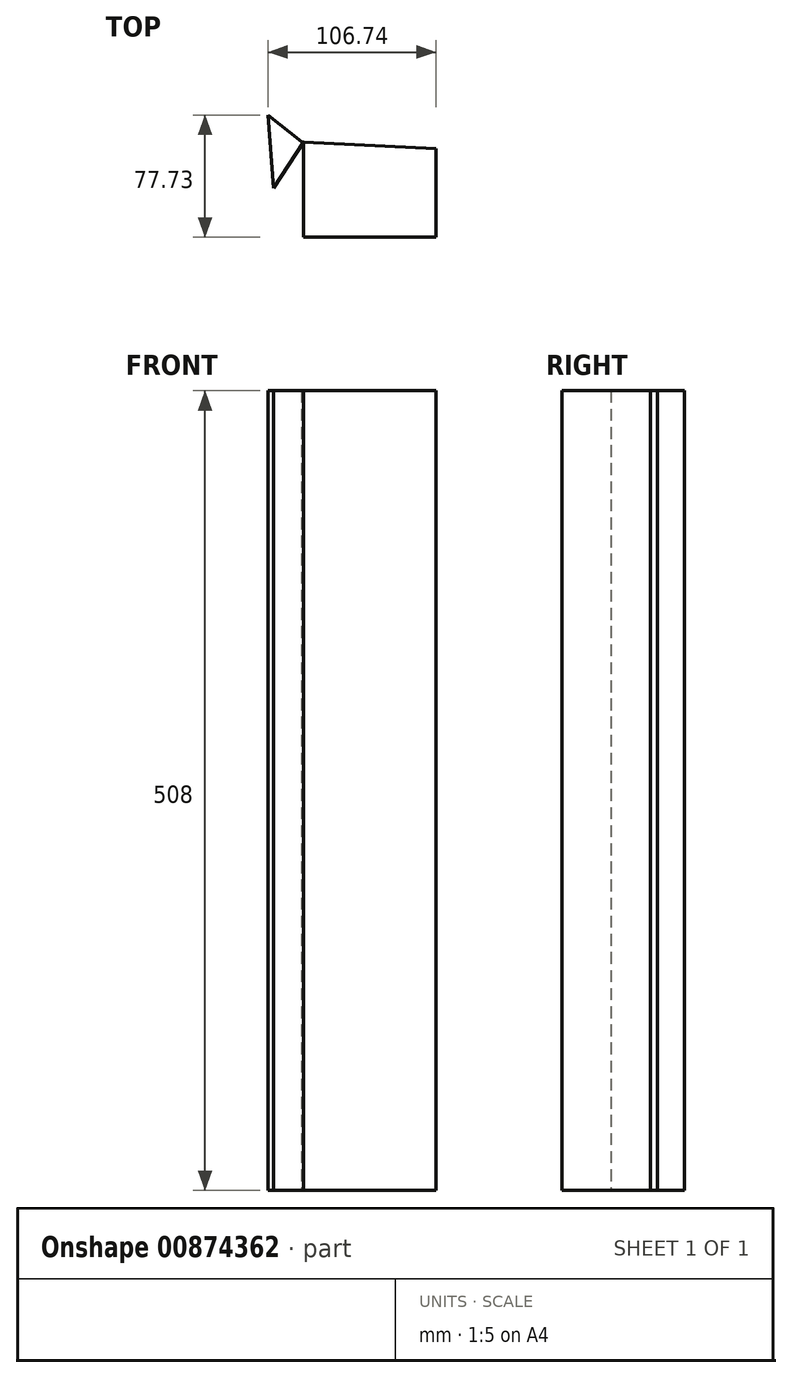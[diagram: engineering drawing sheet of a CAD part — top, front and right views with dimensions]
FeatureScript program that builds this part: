
annotation { "Feature Type Name" : "Feature", "Feature Type Description" : "" }
export const myFeature = defineFeature(function(context is Context, id is Id, definition is map)
    precondition{}
    {
        {
            var Q0;
            Q0=qCreatedBy(makeId("Top.planeOp"),FACE);
            var sketch = newSketch(context, id + "F0", { "sketchPlane" : qUnion([Q0])});
            skLineSegment(sketch, "E0", {"start": v(-42.56, 31.57) * mm, "end": v(42.75, 27.2) * mm});
            skLineSegment(sketch, "E1", {"start": v(42.75, 27.2) * mm, "end": v(42.75, -29.1) * mm});
            skLineSegment(sketch, "E2", {"start": v(42.75, -29.1) * mm, "end": v(-41.24, -29.1) * mm});
            skLineSegment(sketch, "E3", {"start": v(-41.24, -29.1) * mm, "end": v(-41.24, 31.57) * mm});
            skLineSegment(sketch, "E4", {"start": v(-41.24, 31.57) * mm, "end": v(-60.39, 2.18) * mm});
            skLineSegment(sketch, "E5", {"start": v(-60.39, 2.18) * mm, "end": v(-63.99, 48.63) * mm});
            skLineSegment(sketch, "E6", {"start": v(-63.99, 48.63) * mm, "end": v(-42.56, 31.57) * mm});
            skSolve(sketch);
        }
        {
            var Q0;
            Q0 = qSketchRegion(id + "F0", true);
            extrude(context, id + "F1", {"entities" : qUnion([Q0]), "depth" : 508 * mm, "offsetDistance" : 25.4 * mm});
        }
    });
